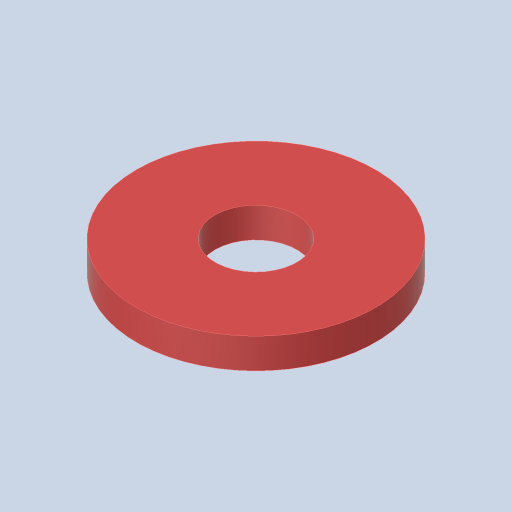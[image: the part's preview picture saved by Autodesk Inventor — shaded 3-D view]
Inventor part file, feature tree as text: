
AUTODESK INVENTOR PART (.ipt)
format: ipt  version: 2023.4 (Build 274418000, 418)  size: 89,088 bytes
history: native  units: in
note: dims shown in document units (in); Inventor stores cm internally (conversion verified against a paired STEP export)
features: extrude x1, sketch x1
ambient origin geometry x8: Origin, YZ Plane, XZ Plane, XY Plane, X Axis, Y Axis, Z Axis, Center Point
bodies: Solid1 (feature_tree)
feature tree (2):
  extrude  "Extrusion1"  Depth=0.11in
  sketch  "Sketch1"  dims[d0=0.3in d1=0.875in d2=0.11in d3=0.0in]
